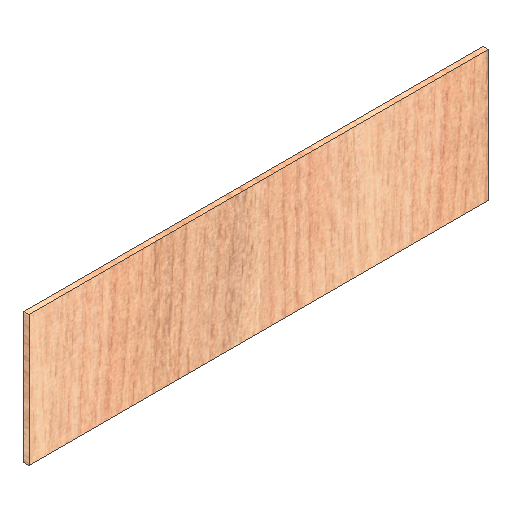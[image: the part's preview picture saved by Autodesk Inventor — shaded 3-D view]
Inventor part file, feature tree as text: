
AUTODESK INVENTOR PART (.ipt)
format: ipt  version: 2021 (Build 250183000, 183)  size: 259,584 bytes
history: native  units: mm
features: extrude x1, sketch x1
ambient origin geometry x8: Origin, YZ Plane, XZ Plane, XY Plane, X Axis, Y Axis, Z Axis, Center Point
bodies: Solid1 (feature_tree)
feature tree (2):
  extrude  "Extrusion1"  Depth=351.11mm
  sketch  "Sketch1"  dims[d0=100.0mm d1=351.11mm d2=4.0mm d3=0.0mm]
